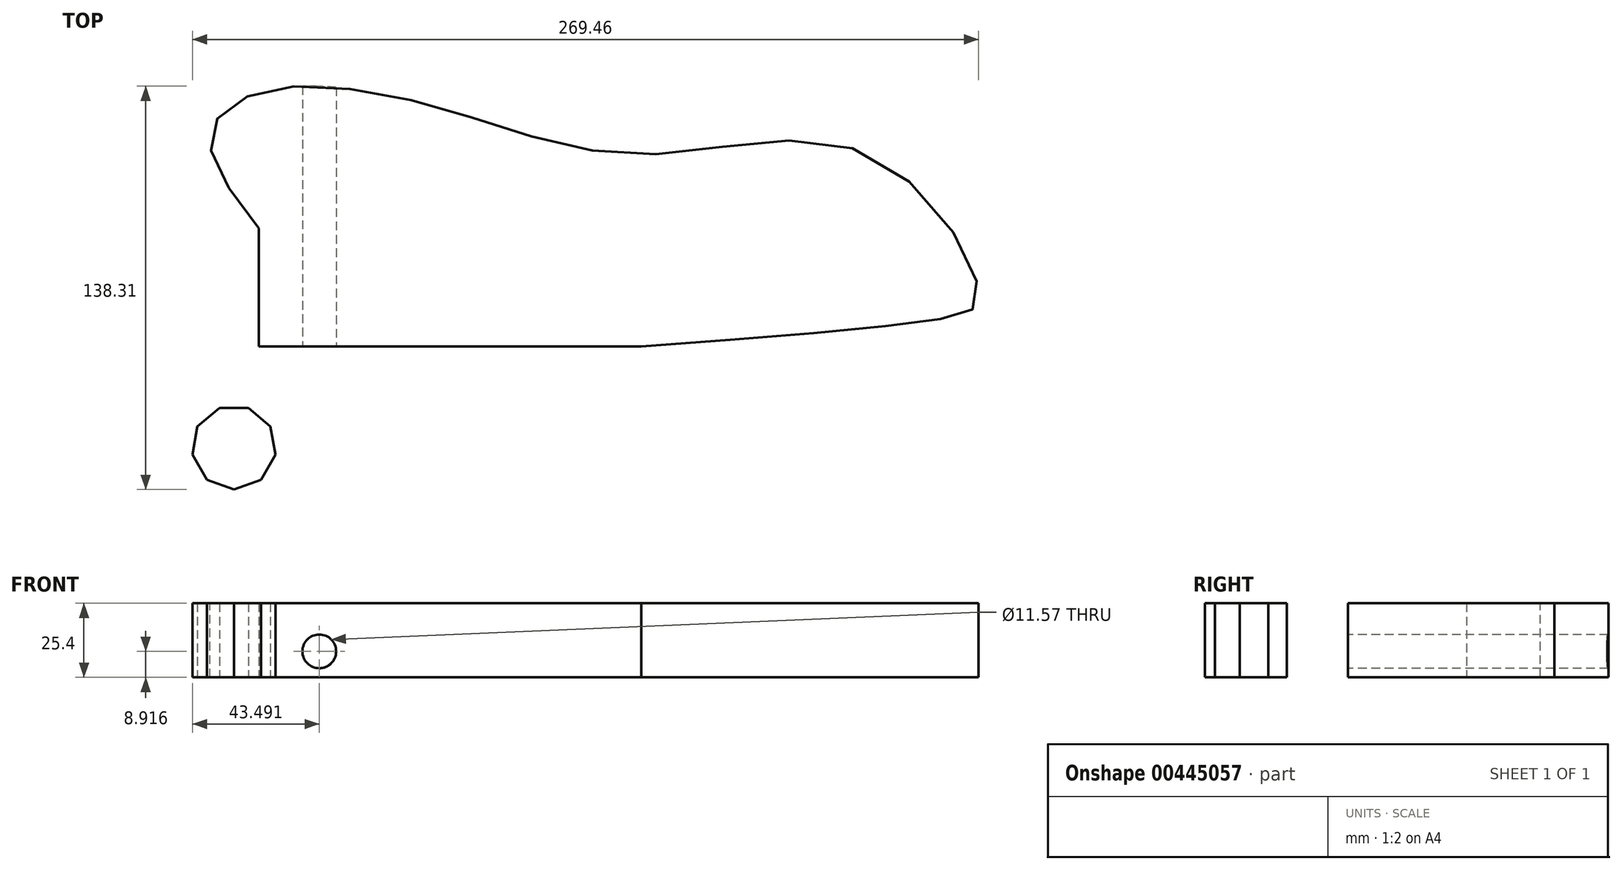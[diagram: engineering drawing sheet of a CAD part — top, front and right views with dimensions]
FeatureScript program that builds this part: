
annotation { "Feature Type Name" : "Feature", "Feature Type Description" : "" }
export const myFeature = defineFeature(function(context is Context, id is Id, definition is map)
    precondition{}
    {
        {
            var Q0;
            Q0=qCreatedBy(makeId("Top.planeOp"),FACE);
            var sketch = newSketch(context, id + "F0", { "sketchPlane" : qUnion([Q0])});
            skLineSegment(sketch, "E0.bottom", {"start": v(-131.1, -40.62) * mm, "end": v(0, -40.62) * mm});
            skLineSegment(sketch, "E0.top", {"start": v(-131.1, 0) * mm, "end": v(0, 0) * mm});
            skLineSegment(sketch, "E0.left", {"start": v(-131.1, -40.62) * mm, "end": v(-131.1, 0) * mm});
            skLineSegment(sketch, "E0.right", {"start": v(0, -40.62) * mm, "end": v(0, 0) * mm});
            skFitSpline(sketch, "E1", {"points": [v(-131.1, 0) * mm, v(-147.78, 30.9) * mm, v(-131.1, 46.57) * mm, v(-71.23, 41.85) * mm, v(0, 25.26) * mm, v(79.05, 24.77) * mm, v(115.58, -23.52) * mm, v(103.52, -31.05) * mm, v(0, -40.62) * mm], "startDerivative": vector(-253.27, 321.74) * mm, "endDerivative": vector(-709.2, -53.94) * mm});
            skCircle(sketch, "E2.cCircle", {"center": v(-139.63, -75.17) * mm, "radius": 13.58 * mm, "construction": true});
            skLineSegment(sketch, "E2.0", {"start": v(-144.58, -61.6) * mm, "end": v(-134.7, -61.6) * mm});
            skLineSegment(sketch, "E2.1", {"start": v(-134.7, -61.6) * mm, "end": v(-127.12, -67.95) * mm});
            skLineSegment(sketch, "E2.2", {"start": v(-127.12, -67.95) * mm, "end": v(-125.4, -77.68) * mm});
            skLineSegment(sketch, "E2.3", {"start": v(-125.4, -77.68) * mm, "end": v(-130.35, -86.24) * mm});
            skLineSegment(sketch, "E2.4", {"start": v(-130.35, -86.24) * mm, "end": v(-139.63, -89.62) * mm});
            skLineSegment(sketch, "E2.5", {"start": v(-139.63, -89.62) * mm, "end": v(-148.92, -86.24) * mm});
            skLineSegment(sketch, "E2.6", {"start": v(-148.92, -86.24) * mm, "end": v(-153.86, -77.68) * mm});
            skLineSegment(sketch, "E2.7", {"start": v(-153.86, -77.68) * mm, "end": v(-152.15, -67.95) * mm});
            skLineSegment(sketch, "E2.8", {"start": v(-152.15, -67.95) * mm, "end": v(-144.58, -61.6) * mm});
            skPoint(sketch, "E2.0.midPoint", {"position": v(-139.63, -61.6) * mm});
            skSolve(sketch);
        }
        {
            var Q0;
            Q0=makeQuery(id+"F0.imprint","IMPRINT",FACE,{"disambiguationData":[TD([[makeQuery(id+"F0.imprint","IMPRINT",EDGE,{"derivedFrom":sQuery(id+"F0.wireOp",EDGE,"E2.0")}),-1.0]])]});
            var Q1;
            Q1=makeQuery(id+"F0.imprint","IMPRINT",FACE,{"disambiguationData":[TD([[makeQuery(id+"F0.imprint","IMPRINT",EDGE,{"derivedFrom":sQuery(id+"F0.wireOp",EDGE,"E0.top")}),1.0]])]});
            var Q2;
            Q2=makeQuery(id+"F0.imprint","IMPRINT",FACE,{"disambiguationData":[TD([[makeQuery(id+"F0.imprint","IMPRINT",EDGE,{"derivedFrom":sQuery(id+"F0.wireOp",EDGE,"E0.bottom")}),1.0]])]});
            extrude(context, id + "F1", {"entities" : qUnion([Q0, Q1, Q2]), "depth" : 25.4 * mm});
        }
        {
            var Q0;
            Q0=makeQuery(id+"F1.opExtrude","SWEPT_FACE",FACE,{"disambiguationData":[OSD([sQuery(id+"F0.wireOp",EDGE,"E0.bottom")])]});
            var sketch = newSketch(context, id + "F2", { "sketchPlane" : qUnion([Q0])});
            skCircle(sketch, "E3", {"center": v(-110.37, 8.92) * mm, "radius": 5.78 * mm});
            skSolve(sketch);
        }
        {
            var Q0;
            Q0=makeQuery(id+"F2.imprint","IMPRINT",FACE,{"disambiguationData":[TD([[makeQuery(id+"F2.imprint","IMPRINT",EDGE,{"derivedFrom":sQuery(id+"F2.wireOp",EDGE,"E3")}),1.0]])]});
            extrude(context, id + "F3", {"entities" : qUnion([Q0]), "operationType" : NewBodyOperationType.REMOVE, "endBound" : BoundingType.THROUGH_ALL, "oppositeDirection" : true, "depth" : 25.4 * mm});
        }
    });
